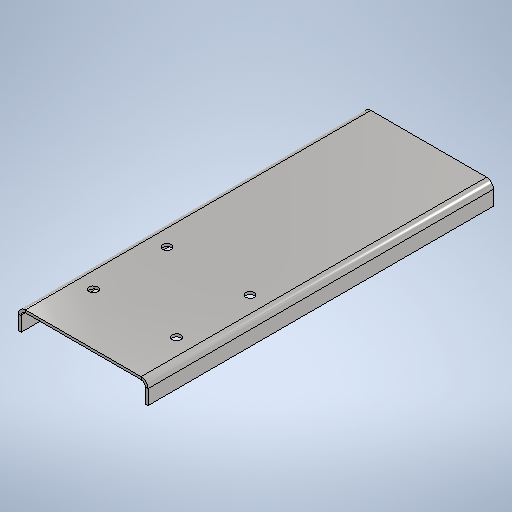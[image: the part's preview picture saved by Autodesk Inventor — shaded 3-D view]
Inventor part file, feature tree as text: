
AUTODESK INVENTOR PART (.ipt)
format: ipt  version: 2025 (Build 290162010, 162A)  size: 343,040 bytes
history: native  units: mm
features: sheet_metal_op x4, sketch x4, other x3, extrude x2, pattern_linear x1
ambient origin geometry x8: Origin, YZ Plane, XZ Plane, XY Plane, X Axis, Y Axis, Z Axis, Center Point
bodies: Body1 (feature_tree)
feature tree (14):
  sheet_metal_op  "Face2"
  extrude  "Extrusion2"  Depth=400.0mm
  sheet_metal_op  "Flange5"
  extrude  "Extrusion5"  Depth=10.0mm
  pattern_linear  "Rectangular Pattern2"  Spacing1=96.0mm  [1 undecoded]
  sketch  "Sketch4"  dims[d24=150.0mm d25=400.0mm]
  other  "Plate4"
  sketch  "Sketch7"  dims[d26=3.0mm d41=10.0mm]
  sketch  "Sketch9"  dims[d44=0.0mm d45=0.0mm]
  other  "Plate7"
  sheet_metal_op  "Bend5"
  sheet_metal_op  "Corner5"
  sketch  "Sketch12"  dims[d46=85.0mm d57=96.0mm d60=3.0mm d61=1.5mm d62=6.0mm d63=5.0mm d64=25.0mm d65=90.0deg d66=5.0mm d67=12.0mm d68=3.0mm d69=5.0mm d70=145.0mm d86=10.125mm d87=50.0mm d88=6.0mm d89=0.0mm d90=0.0mm d91=40.0mm d93=100.0mm d94=20.0mm d96=169.75mm d78=0.5mm d79=0.872665mm d80=0.5mm d81=0.872665mm]
  other  "Definition1"
note: 1 required parameter value undecoded (feature->parameter linkage not recoverable at this tier; creation-order binding heuristic only, values carry confidence <= 0.55)
